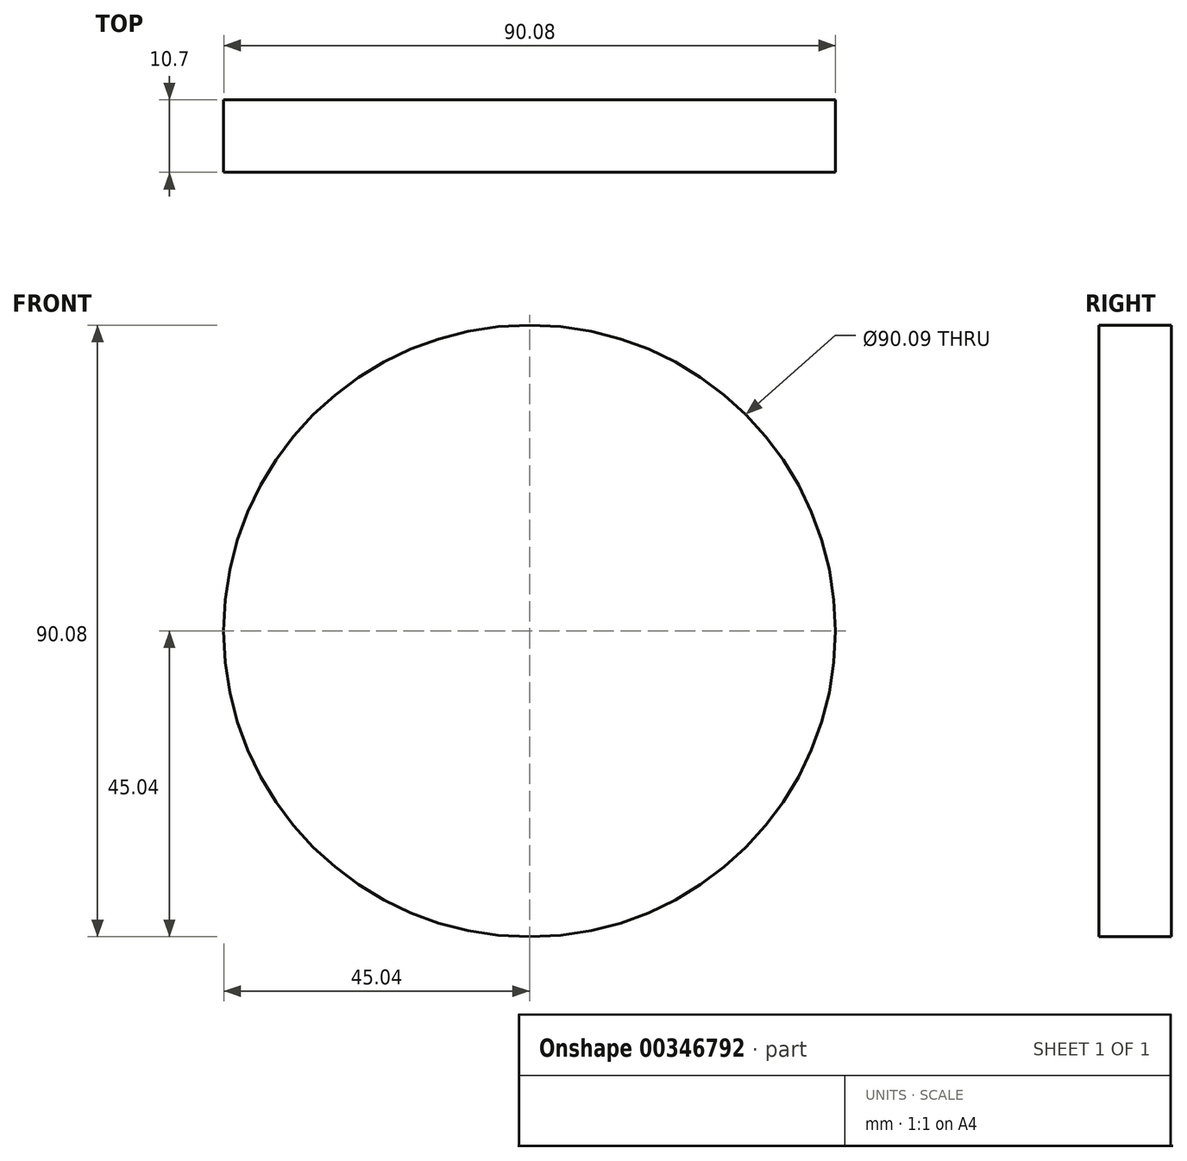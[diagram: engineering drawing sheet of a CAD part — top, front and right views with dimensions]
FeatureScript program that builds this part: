
annotation { "Feature Type Name" : "Feature", "Feature Type Description" : "" }
export const myFeature = defineFeature(function(context is Context, id is Id, definition is map)
    precondition{}
    {
        {
            var Q0;
            Q0=qCreatedBy(makeId("Front.planeOp"),FACE);
            var sketch = newSketch(context, id + "F0", { "sketchPlane" : qUnion([Q0])});
            skCircle(sketch, "E0", {"center": v(0, 0) * mm, "radius": 45.04 * mm});
            skSolve(sketch);
        }
        {
            var Q0;
            Q0=sQuery(id+"F0.wireOp",EDGE,"E0");
            extrude(context, id + "F1", {"bodyType" : ToolBodyType.SURFACE, "surfaceEntities" : qUnion([Q0]), "oppositeDirection" : true, "depth" : 10.7 * mm});
        }
    });
